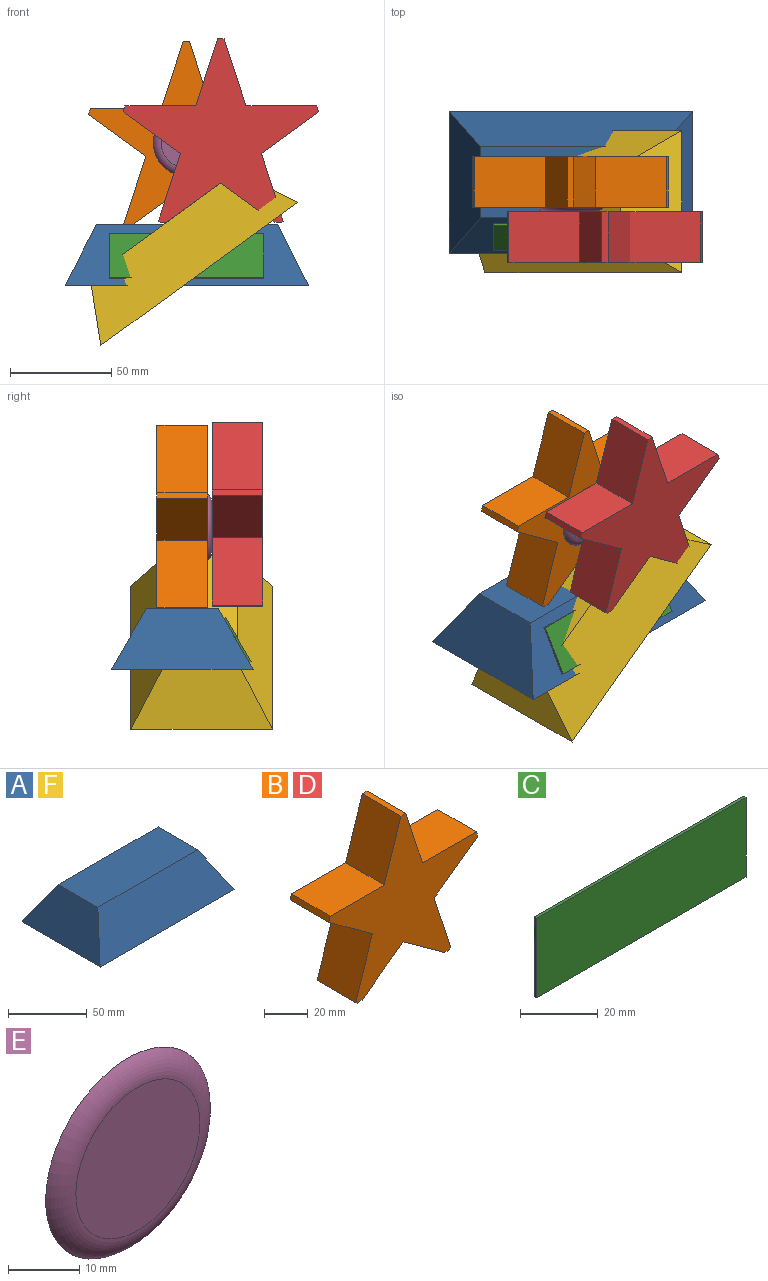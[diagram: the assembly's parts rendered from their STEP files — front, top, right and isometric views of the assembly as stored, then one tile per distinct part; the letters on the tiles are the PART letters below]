
ASSEMBLY  parts=6 mates=2
PART A: 6 faces, bbox 120x70x30 mm
  f0: plane 120x70mm, normal (0,0,-1), area 8400mm2, adj f2,f3,f4,f5
  f1: plane 89.43x35.36mm, normal (0,0,1), area 3162.1mm2, adj f2,f3,f4,f5
  f2: plane 120x30mm, normal (0,0.87,0.5), area 3627.4mm2, adj f0,f1,f4,f5
  f3: plane 120x30mm, normal (0,-0.87,0.5), area 3627.4mm2, adj f0,f1,f4,f5
  f4: plane 70x30mm, normal (-0.89,0,0.45), area 1773.7mm2, adj f0,f1,f2,f3
  f5: plane 70x30mm, normal (0.89,0,0.45), area 1773.7mm2, adj f0,f1,f2,f3
PART B: 19 faces, bbox 96.5x25x90.6 mm
  f0: plane 33.25x25mm, normal (-0.95,0,0.31), area 874mm2, adj f1,f10,f11,f16
  f1: plane 34.96x25mm, normal (0,0,1), area 874mm2, adj f0,f10,f11,f15
  f2: plane 28.28x25mm, normal (-0.59,0,-0.81), area 874mm2, adj f3,f10,f11,f15
  f3: plane 33.25x25mm, normal (-0.95,0,0.31), area 874mm2, adj f2,f10,f11,f13
  f4: plane 26.67x25mm, normal (0.59,0,-0.81), area 824mm2, adj f5,f10,f11,f17
  f5: plane 26.67x25mm, normal (-0.59,0,-0.81), area 824mm2, adj f4,f10,f11,f18
  f6: plane 33.25x25mm, normal (0.95,0,0.31), area 874mm2, adj f7,f10,f11,f12
  f7: plane 28.28x25mm, normal (0.59,0,-0.81), area 874mm2, adj f6,f10,f11,f14
  f8: plane 34.96x25mm, normal (0,0,1), area 874mm2, adj f9,f10,f11,f14
  f9: plane 33.25x25mm, normal (0.95,0,0.31), area 874mm2, adj f8,f10,f11,f16
  f10: plane 96.53x90.63mm, normal (0,-1,0), area 3355.2mm2, adj f0,f1,f2,f3,f4,f5,f6,f7
  f11: plane 96.53x90.63mm, normal (0,1,0), area 3355.2mm2, adj f0,f1,f2,f3,f4,f5,f6,f7
  f12: plane 25x0.88mm, normal (0.59,0,-0.81), area 27.3mm2, adj f6,f10,f11,f18
  f13: plane 25x0.88mm, normal (-0.59,0,-0.81), area 27.3mm2, adj f3,f10,f11,f17
  f14: plane 25x2.94mm, normal (0.95,0,0.31), area 77.3mm2, adj f7,f8,f10,f11
  f15: plane 25x2.94mm, normal (-0.95,0,0.31), area 77.3mm2, adj f1,f2,f10,f11
  f16: plane 25x3.09mm, normal (0,0,1), area 77.3mm2, adj f0,f9,f10,f11
  f17: plane 25x3.24mm, normal (0,0,-1), area 80.9mm2, adj f4,f10,f11,f13
  f18: plane 25x3.24mm, normal (0,0,-1), area 80.9mm2, adj f5,f10,f11,f12
PART C: 6 faces, bbox 76x1x25 mm
  f0: plane 76x1mm, normal (0,0,-1), area 76mm2, adj f1,f3,f4,f5
  f1: plane 25x1mm, normal (1,0,0), area 25mm2, adj f0,f2,f4,f5
  f2: plane 76x1mm, normal (0,0,1), area 76mm2, adj f1,f3,f4,f5
  f3: plane 25x1mm, normal (-1,0,0), area 25mm2, adj f0,f2,f4,f5
  f4: plane 76x25mm, normal (0,-1,0), area 1900mm2, adj f0,f1,f2,f3
  f5: plane 76x25mm, normal (0,1,0), area 1900mm2, adj f0,f1,f2,f3
PART D: same geometry as B
PART E: 3 faces, bbox 37.5x5x37.5 mm
  f0: plane 24.66x24.66mm, normal (0,-1,0), area 477.4mm2, adj f2
  f1: plane 32.66x32.66mm, normal (0,1,0), area 837.5mm2, adj f2
  f2: torus R=12.33mm, axis (0,1,0), area 422mm2, adj f0,f1
PART F: same geometry as A
PLACE A t=(-8.28,26.59,-27.66)mm
PLACE B t=(-8.57,39.12,27.63)mm
PLACE C rot(axis=(-1,0,0),30deg) t=(-8.28,-0.17,-28.39)mm
PLACE D t=(8.46,11.85,28.86)mm
PLACE E t=(-8.57,14.12,27.68)mm
PLACE F rot(axis=(0,-1,0),36deg) t=(-11,17.03,-24.83)mm
MATE fastened C.f5 <-> A.f3  axis (0,0.87,-0.5) through (-8.28,-0.17,-28.39)mm
MATE fastened B.f10 <-> E.f2  axis (0,-1,0) through (-8.57,14.12,27.68)mm
